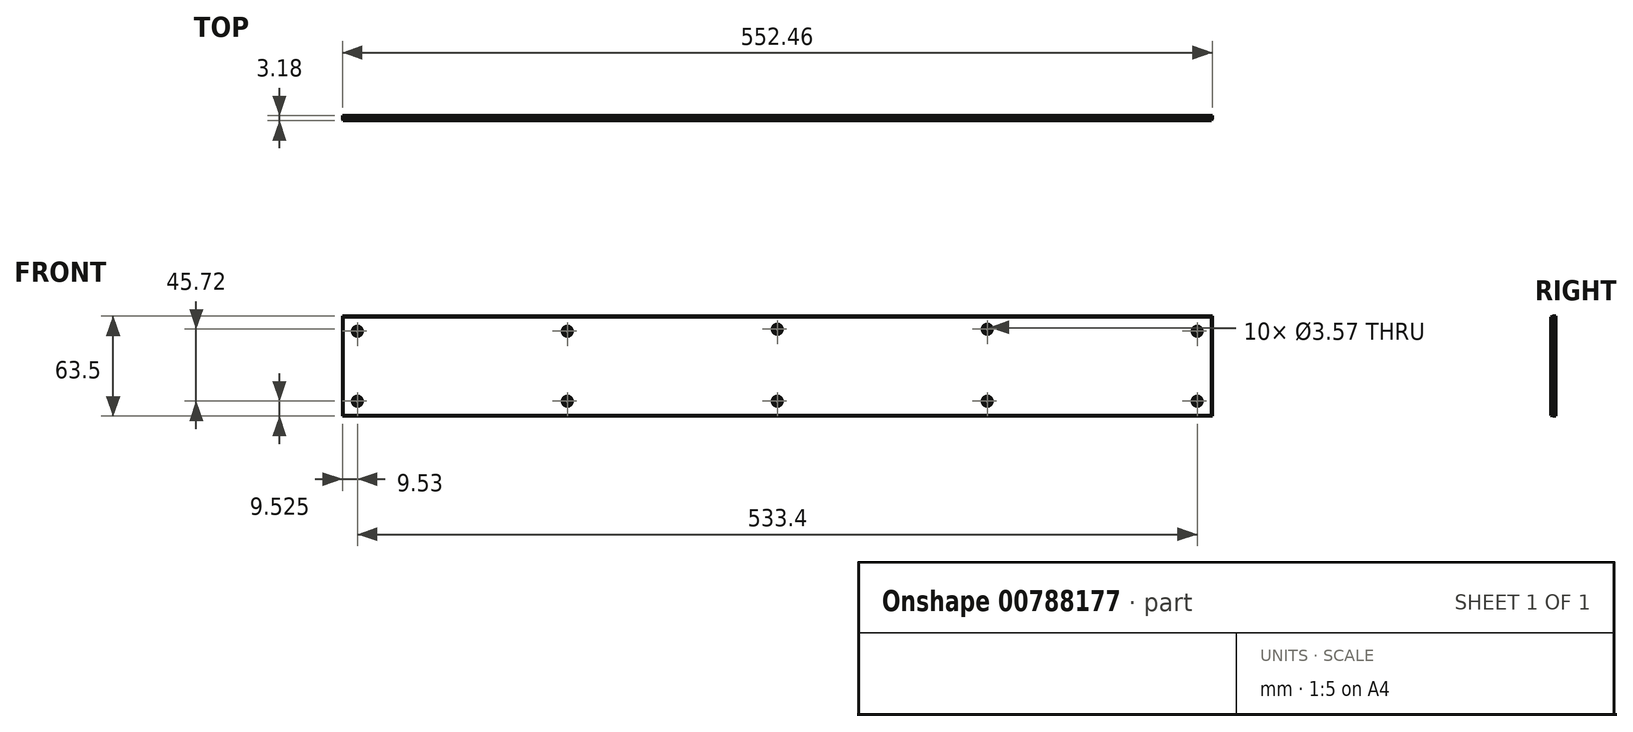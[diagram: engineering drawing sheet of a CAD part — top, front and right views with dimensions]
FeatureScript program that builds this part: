
annotation { "Feature Type Name" : "Feature", "Feature Type Description" : "" }
export const myFeature = defineFeature(function(context is Context, id is Id, definition is map)
    precondition{}
    {
        {
            var Q0;
            Q0=qCreatedBy(makeId("Front.planeOp"),FACE);
            var sketch = newSketch(context, id + "F0", { "sketchPlane" : qUnion([Q0])});
            skLineSegment(sketch, "E0.bottom", {"start": v(276.23, 31.75) * mm, "end": v(-276.23, 31.75) * mm});
            skLineSegment(sketch, "E0.top", {"start": v(276.23, -31.75) * mm, "end": v(-276.23, -31.75) * mm});
            skLineSegment(sketch, "E0.left", {"start": v(276.23, 31.75) * mm, "end": v(276.23, -31.75) * mm});
            skLineSegment(sketch, "E0.right", {"start": v(-276.23, 31.75) * mm, "end": v(-276.23, -31.75) * mm});
            skPoint(sketch, "E0.middle", {"position": v(0, 0) * mm});
            skCircle(sketch, "E1", {"center": v(-266.7, 22.22) * mm, "radius": 1.63 * mm});
            skCircle(sketch, "E2", {"center": v(-131.45, 22.22) * mm, "radius": 1.63 * mm});
            skCircle(sketch, "E3", {"center": v(0, 23.5) * mm, "radius": 1.63 * mm});
            skCircle(sketch, "E4", {"center": v(130.17, 23.5) * mm, "radius": 1.63 * mm});
            skCircle(sketch, "E5", {"center": v(266.7, 22.23) * mm, "radius": 1.63 * mm});
            skCircle(sketch, "E6", {"center": v(-266.7, -22.23) * mm, "radius": 1.63 * mm});
            skCircle(sketch, "E7", {"center": v(-131.44, -22.23) * mm, "radius": 1.63 * mm});
            skCircle(sketch, "E8", {"center": v(0, -22.23) * mm, "radius": 1.63 * mm});
            skCircle(sketch, "E9", {"center": v(130.17, -22.23) * mm, "radius": 1.63 * mm});
            skCircle(sketch, "E10", {"center": v(266.7, -22.23) * mm, "radius": 1.63 * mm});
            skLineSegment(sketch, "E11.bottom", {"start": v(254, -12.7) * mm, "end": v(-254, -12.7) * mm, "construction": true});
            skLineSegment(sketch, "E11.top", {"start": v(254, 12.7) * mm, "end": v(-254, 12.7) * mm, "construction": true});
            skArc(sketch, "E12", {"start": v(-254, 12.7) * mm, "mid": v(-266.7, 0) * mm, "end": v(-254, -12.7) * mm, "construction": true});
            skArc(sketch, "E13", {"start": v(254, -12.7) * mm, "mid": v(266.7, 0) * mm, "end": v(254, 12.7) * mm, "construction": true});
            skSolve(sketch);
        }
        {
            var Q0;
            Q0=makeQuery(id+"F0.imprint","IMPRINT",FACE,{"disambiguationData":[TD([[makeQuery(id+"F0.imprint","IMPRINT",EDGE,{"derivedFrom":sQuery(id+"F0.wireOp",EDGE,"E0.bottom")}),1.0]])]});
            var Q1;
            Q1=makeQuery(id+"F0.imprint","IMPRINT",FACE,{"disambiguationData":[TD([[makeQuery(id+"F0.imprint","IMPRINT",EDGE,{"derivedFrom":sQuery(id+"F0.wireOp",EDGE,"E1")}),1.0]])]});
            var Q2;
            Q2=makeQuery(id+"F0.imprint","IMPRINT",FACE,{"disambiguationData":[TD([[makeQuery(id+"F0.imprint","IMPRINT",EDGE,{"derivedFrom":sQuery(id+"F0.wireOp",EDGE,"E2")}),1.0]])]});
            var Q3;
            Q3=makeQuery(id+"F0.imprint","IMPRINT",FACE,{"disambiguationData":[TD([[makeQuery(id+"F0.imprint","IMPRINT",EDGE,{"derivedFrom":sQuery(id+"F0.wireOp",EDGE,"E3")}),1.0]])]});
            var Q4;
            Q4=makeQuery(id+"F0.imprint","IMPRINT",FACE,{"disambiguationData":[TD([[makeQuery(id+"F0.imprint","IMPRINT",EDGE,{"derivedFrom":sQuery(id+"F0.wireOp",EDGE,"E4")}),1.0]])]});
            var Q5;
            Q5=makeQuery(id+"F0.imprint","IMPRINT",FACE,{"disambiguationData":[TD([[makeQuery(id+"F0.imprint","IMPRINT",EDGE,{"derivedFrom":sQuery(id+"F0.wireOp",EDGE,"E5")}),1.0]])]});
            var Q6;
            Q6=makeQuery(id+"F0.imprint","IMPRINT",FACE,{"disambiguationData":[TD([[makeQuery(id+"F0.imprint","IMPRINT",EDGE,{"derivedFrom":sQuery(id+"F0.wireOp",EDGE,"E6")}),1.0]])]});
            var Q7;
            Q7=makeQuery(id+"F0.imprint","IMPRINT",FACE,{"disambiguationData":[TD([[makeQuery(id+"F0.imprint","IMPRINT",EDGE,{"derivedFrom":sQuery(id+"F0.wireOp",EDGE,"E7")}),1.0]])]});
            var Q8;
            Q8=makeQuery(id+"F0.imprint","IMPRINT",FACE,{"disambiguationData":[TD([[makeQuery(id+"F0.imprint","IMPRINT",EDGE,{"derivedFrom":sQuery(id+"F0.wireOp",EDGE,"E8")}),1.0]])]});
            var Q9;
            Q9=makeQuery(id+"F0.imprint","IMPRINT",FACE,{"disambiguationData":[TD([[makeQuery(id+"F0.imprint","IMPRINT",EDGE,{"derivedFrom":sQuery(id+"F0.wireOp",EDGE,"E9")}),1.0]])]});
            var Q10;
            Q10=makeQuery(id+"F0.imprint","IMPRINT",FACE,{"disambiguationData":[TD([[makeQuery(id+"F0.imprint","IMPRINT",EDGE,{"derivedFrom":sQuery(id+"F0.wireOp",EDGE,"E10")}),1.0]])]});
            extrude(context, id + "F1", {"entities" : qUnion([Q0, Q1, Q2, Q3, Q4, Q5, Q6, Q7, Q8, Q9, Q10]), "oppositeDirection" : true, "depth" : 3.17 * mm, "offsetDistance" : 25.4 * mm});
        }
        {
            var Q0;
            Q0=makeQuery(id+"F1.opExtrude","CAP_FACE",FACE,{"disambiguationData":[OSD([sQuery(id+"F0.wireOp",EDGE,"E0.bottom"),sQuery(id+"F0.wireOp",EDGE,"E0.top"),sQuery(id+"F0.wireOp",EDGE,"E0.left"),sQuery(id+"F0.wireOp",EDGE,"E0.right")])],"isStart":true});
            var sketch = newSketch(context, id + "F2", { "sketchPlane" : qUnion([Q0])});
            skLineSegment(sketch, "E14.bottom", {"start": v(276.23, 31.75) * mm, "end": v(-276.23, 31.75) * mm});
            skLineSegment(sketch, "E14.top", {"start": v(276.23, -31.75) * mm, "end": v(-276.23, -31.75) * mm});
            skLineSegment(sketch, "E14.left", {"start": v(276.23, 31.75) * mm, "end": v(276.23, -31.75) * mm});
            skLineSegment(sketch, "E14.right", {"start": v(-276.23, 31.75) * mm, "end": v(-276.23, -31.75) * mm});
            skPoint(sketch, "E14.middle", {"position": v(0, 0) * mm});
            skCircle(sketch, "E15", {"center": v(-266.7, 22.22) * mm, "radius": 1.63 * mm});
            skCircle(sketch, "E16", {"center": v(-133.35, 22.22) * mm, "radius": 1.63 * mm});
            skCircle(sketch, "E17", {"center": v(0, 23.5) * mm, "radius": 1.63 * mm});
            skCircle(sketch, "E18", {"center": v(133.35, 23.5) * mm, "radius": 1.63 * mm});
            skCircle(sketch, "E19", {"center": v(266.7, 22.23) * mm, "radius": 1.63 * mm});
            skCircle(sketch, "E20", {"center": v(-266.7, -22.23) * mm, "radius": 1.63 * mm});
            skCircle(sketch, "E21", {"center": v(-133.35, -22.23) * mm, "radius": 1.63 * mm});
            skCircle(sketch, "E22", {"center": v(0, -22.23) * mm, "radius": 1.63 * mm});
            skCircle(sketch, "E23", {"center": v(133.35, -22.23) * mm, "radius": 1.63 * mm});
            skCircle(sketch, "E24", {"center": v(266.7, -22.23) * mm, "radius": 1.63 * mm});
            skLineSegment(sketch, "E25.bottom", {"start": v(254, -12.7) * mm, "end": v(-254, -12.7) * mm, "construction": true});
            skLineSegment(sketch, "E25.top", {"start": v(254, 12.7) * mm, "end": v(-254, 12.7) * mm, "construction": true});
            skArc(sketch, "E26", {"start": v(-254, 12.7) * mm, "mid": v(-266.7, 0) * mm, "end": v(-254, -12.7) * mm, "construction": true});
            skArc(sketch, "E27", {"start": v(254, -12.7) * mm, "mid": v(266.7, 0) * mm, "end": v(254, 12.7) * mm, "construction": true});
            skSolve(sketch);
        }
        {
            var Q0;
            Q0=sQuery(id+"F2.wireOp",VERTEX,"E15.center");
            var Q1;
            Q1=sQuery(id+"F2.wireOp",VERTEX,"E16.center");
            var Q2;
            Q2=sQuery(id+"F2.wireOp",VERTEX,"E17.center");
            var Q3;
            Q3=sQuery(id+"F2.wireOp",VERTEX,"E20.center");
            var Q4;
            Q4=sQuery(id+"F2.wireOp",VERTEX,"E21.center");
            var Q5;
            Q5=sQuery(id+"F2.wireOp",VERTEX,"E22.center");
            var Q6;
            Q6=sQuery(id+"F2.wireOp",VERTEX,"E18.center");
            var Q7;
            Q7=sQuery(id+"F2.wireOp",VERTEX,"E23.center");
            var Q8;
            Q8=sQuery(id+"F2.wireOp",VERTEX,"E24.center");
            var Q9;
            Q9=sQuery(id+"F2.wireOp",VERTEX,"E19.center");
            var Q10;
            Q10=makeQuery(id+"F1.opExtrude","SWEPT_BODY",BODY,{"disambiguationData":[OSD([sQuery(id+"F0.wireOp",EDGE,"E0.bottom"),sQuery(id+"F0.wireOp",EDGE,"E0.top"),sQuery(id+"F0.wireOp",EDGE,"E0.left"),sQuery(id+"F0.wireOp",EDGE,"E0.right")])]});
            hole(context, id + "F3", {"style" : HoleStyle.C_SINK, "endStyle" : HoleEndStyle.THROUGH, "holeDiameter" : 3.57 * mm, "cSinkDiameter" : 6.35 * mm, "cSinkAngle" : 100 * degree, "majorDiameter" : 6.35 * mm, "isTappedThrough" : true, "tappedDepth" : 12.7 * mm, "tapClearance" : 3, "startFromSketch" : true, "locations" : qUnion([Q0, Q1, Q2, Q3, Q4, Q5, Q6, Q7, Q8, Q9]), "scope" : qUnion([Q10])});
        }
        {
            var Q0;
            Q0=makeQuery(id+"F1.opExtrude","CAP_EDGE",EDGE,{"disambiguationData":[OSD([sQuery(id+"F0.wireOp",EDGE,"E0.bottom")])],"isStart":true});
            var Q1;
            Q1=makeQuery(id+"F1.opExtrude","CAP_EDGE",EDGE,{"disambiguationData":[OSD([sQuery(id+"F0.wireOp",EDGE,"E0.left")])],"isStart":true});
            var Q2;
            Q2=makeQuery(id+"F1.opExtrude","CAP_EDGE",EDGE,{"disambiguationData":[OSD([sQuery(id+"F0.wireOp",EDGE,"E0.top")])],"isStart":true});
            var Q3;
            Q3=makeQuery(id+"F1.opExtrude","CAP_EDGE",EDGE,{"disambiguationData":[OSD([sQuery(id+"F0.wireOp",EDGE,"E0.right")])],"isStart":true});
            chamfer(context, id + "F4", {"entities" : qUnion([Q0, Q1, Q2, Q3]), "chamferType" : ChamferType.OFFSET_ANGLE, "width" : 1.59 * mm, "oppositeDirection" : true, "angle" : 15 * degree, "tangentPropagation" : true});
        }
    });
